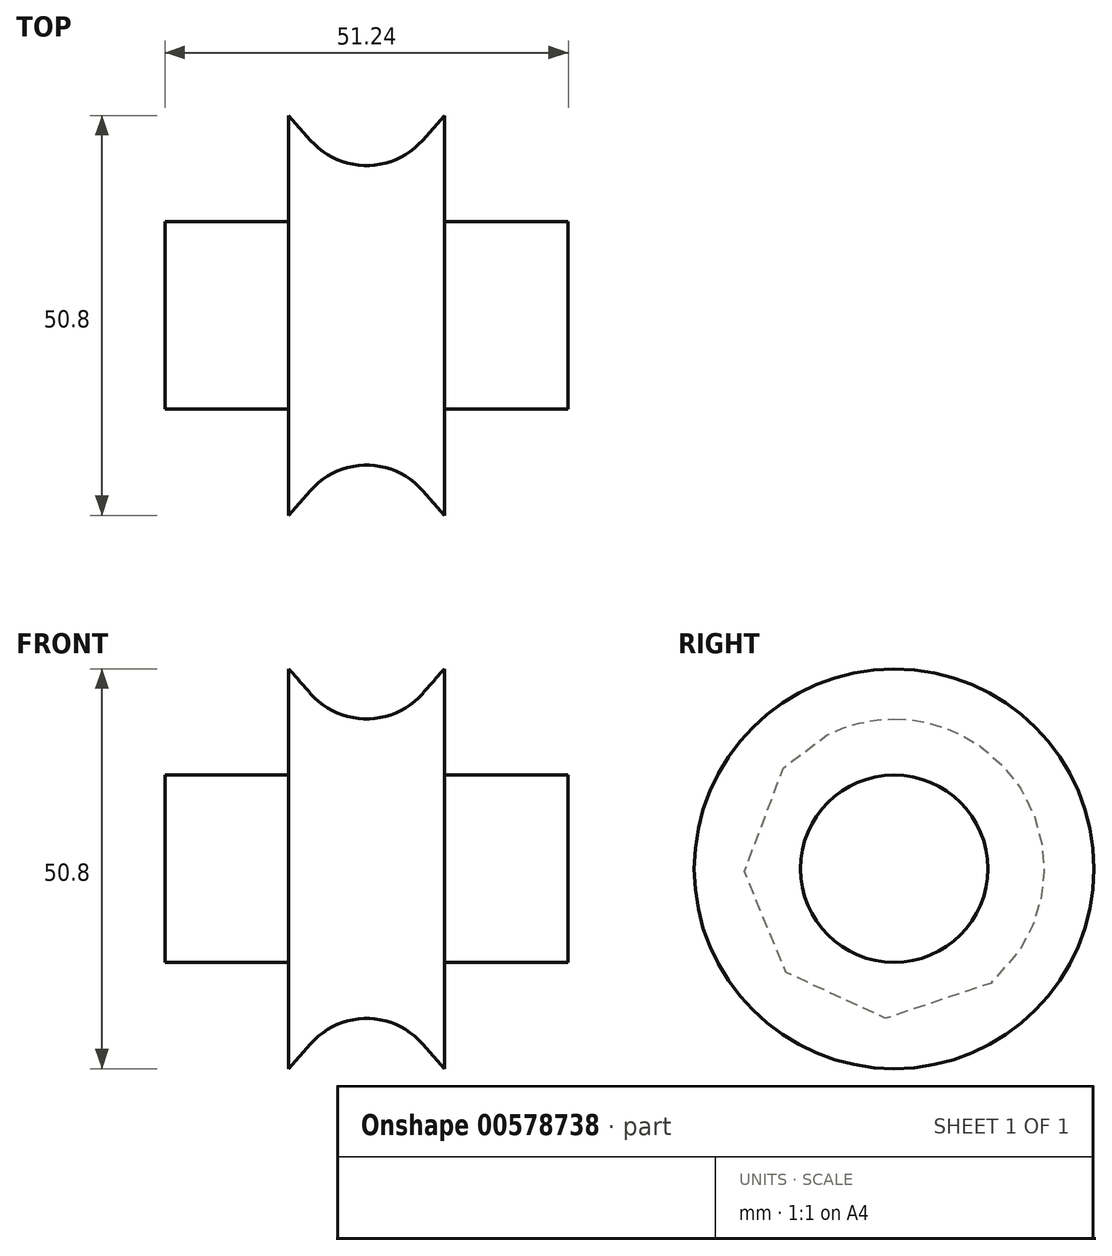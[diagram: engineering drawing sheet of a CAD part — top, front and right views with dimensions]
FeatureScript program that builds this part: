
annotation { "Feature Type Name" : "Feature", "Feature Type Description" : "" }
export const myFeature = defineFeature(function(context is Context, id is Id, definition is map)
    precondition{}
    {
        {
            var Q0;
            Q0=qCreatedBy(makeId("Front.planeOp"),FACE);
            var sketch = newSketch(context, id + "F0", { "sketchPlane" : qUnion([Q0])});
            skLineSegment(sketch, "E0", {"start": v(0, -16.5) * mm, "end": v(0, 68.1) * mm, "construction": true});
            skLineSegment(sketch, "E1", {"start": v(25.62, 11.9) * mm, "end": v(9.89, 11.9) * mm});
            skLineSegment(sketch, "E2", {"start": v(9.89, 11.9) * mm, "end": v(9.89, 25.4) * mm});
            skLineSegment(sketch, "E3", {"start": v(9.89, 25.4) * mm, "end": v(7.09, 22.23) * mm});
            skLineSegment(sketch, "E4", {"start": v(25.62, 11.9) * mm, "end": v(25.62, 0) * mm});
            skLineSegment(sketch, "E5", {"start": v(7.09, 22.23) * mm, "end": v(9.89, 25.4) * mm});
            skLineSegment(sketch, "E6.MirrorCS", {"start": v(-25.62, 11.9) * mm, "end": v(-25.62, 0) * mm});
            skLineSegment(sketch, "E7.MirrorCS", {"start": v(-25.62, 11.9) * mm, "end": v(-9.89, 11.9) * mm});
            skLineSegment(sketch, "E8.MirrorCS", {"start": v(-9.89, 11.9) * mm, "end": v(-9.89, 25.4) * mm});
            skLineSegment(sketch, "E9.MirrorCS", {"start": v(-7.09, 22.23) * mm, "end": v(-9.89, 25.4) * mm});
            skArc(sketch, "E10", {"start": v(-7.09, 22.23) * mm, "mid": v(0, 19.03) * mm, "end": v(7.09, 22.23) * mm});
            skLineSegment(sketch, "E11", {"start": v(-25.62, 0) * mm, "end": v(25.62, 0) * mm});
            skSolve(sketch);
        }
        {
            var Q0;
            Q0=makeQuery(id+"F0.imprint","IMPRINT",FACE,{"disambiguationData":[TD([[makeQuery(id+"F0.imprint","IMPRINT",EDGE,{"derivedFrom":sQuery(id+"F0.wireOp",EDGE,"E1")}),1.0]])]});
            var Q1;
            Q1=sQuery(id+"F0.wireOp",EDGE,"E11");
            revolve(context, id + "F1", {"entities" : qUnion([Q0]), "axis" : qUnion([Q1]), "revolveType" : RevolveType.FULL});
        }
    });
